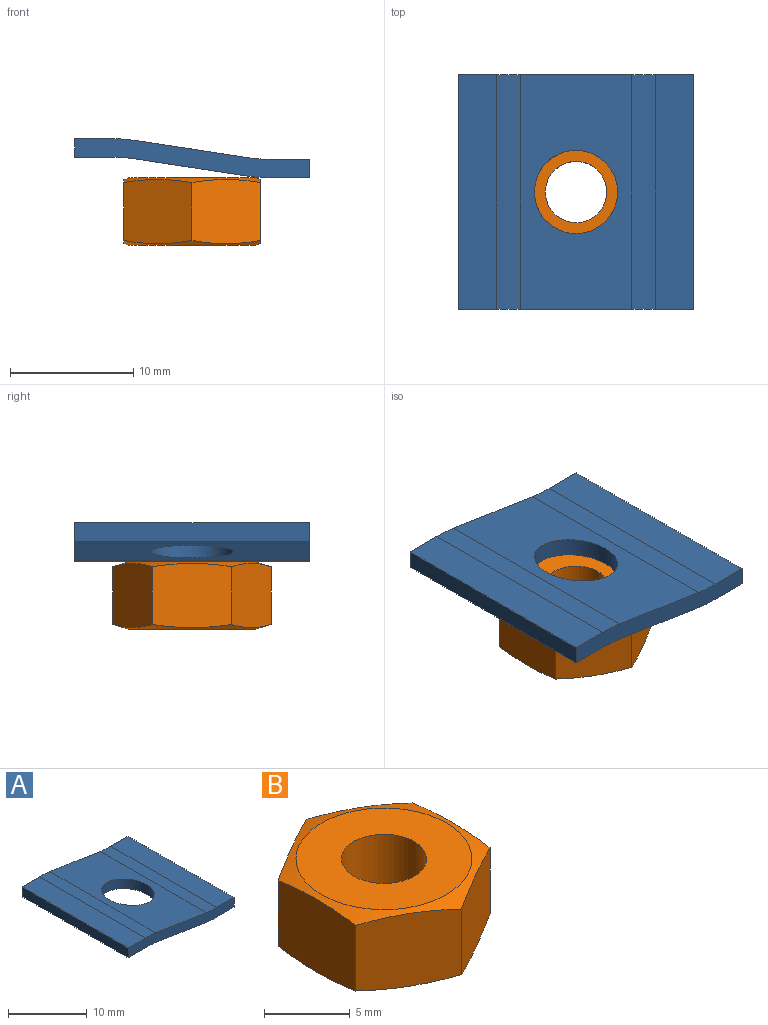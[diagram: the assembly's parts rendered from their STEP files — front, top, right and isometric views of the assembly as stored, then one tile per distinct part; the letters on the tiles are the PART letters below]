
ASSEMBLY  parts=2 mates=2
PART A: 15 faces, bbox 19.1x19.1x3.2 mm
  f0: plane 19.05x3.09mm, normal (0,0,1), area 58.8mm2, adj f1,f8,f9,f13
  f1: plane 19.05x1.5mm, normal (-1,0,0), area 28.5mm2, adj f0,f2,f8,f9
  f2: plane 19.05x3.09mm, normal (0,0,-1), area 58.8mm2, adj f1,f8,f9,f10
  f3: plane 19.05x9.03mm, normal (-0.15,0,-0.99), area 137.9mm2, adj f8,f9,f10,f11,f14
  f4: plane 19.05x3.09mm, normal (0,0,-1), area 58.8mm2, adj f5,f8,f9,f11
  f5: plane 19.05x1.5mm, normal (1,0,0), area 28.5mm2, adj f4,f6,f8,f9
  f6: plane 19.05x3.09mm, normal (0,0,1), area 58.8mm2, adj f5,f8,f9,f12
  f7: plane 19.05x9.03mm, normal (0.15,0,0.99), area 137.9mm2, adj f8,f9,f12,f13,f14
  f8: plane 19.05x3.18mm, normal (0,-1,0), area 28.5mm2, adj f0,f1,f2,f3,f4,f5,f6,f7
  f9: plane 19.05x3.18mm, normal (0,1,0), area 28.5mm2, adj f0,f1,f2,f3,f4,f5,f6,f7
  f10: cylinder r=12.7mm len=19.05mm, axis (0,-1,0), area 36.8mm2, adj f2,f3,f8,f9
  f11: cylinder r=12.7mm len=19.05mm, axis (0,1,0), area 36.8mm2, adj f3,f4,f8,f9
  f12: cylinder r=12.7mm len=19.05mm, axis (0,-1,0), area 36.8mm2, adj f6,f7,f8,f9
  f13: cylinder r=12.7mm len=19.05mm, axis (0,1,0), area 36.8mm2, adj f0,f7,f8,f9
  f14: cylinder r=3.37mm len=6.75mm, axis (0,0,-1), area 31.8mm2, adj f3,f7
PART B: 11 faces, bbox 12.8x12.8x5.5 mm
  f0: plane 6.42x5.22mm, normal (1,0,0), area 32.3mm2, adj f1,f5,f9,f10
  f1: plane 5.56x5.21mm, normal (0.5,-0.87,0), area 32.3mm2, adj f0,f2,f9,f10
  f2: plane 5.56x5.21mm, normal (-0.5,-0.87,0), area 32.3mm2, adj f1,f3,f9,f10
  f3: plane 6.42x5.22mm, normal (-1,0,0), area 32.3mm2, adj f2,f4,f9,f10
  f4: plane 5.56x5.21mm, normal (-0.5,0.87,0), area 32.3mm2, adj f3,f5,f9,f10
  f5: plane 5.56x5.21mm, normal (0.5,0.87,0), area 32.3mm2, adj f0,f4,f9,f10
  f6: cylinder r=2.49mm len=5.46mm, axis (0,0,-1), area 85.4mm2, adj f7,f8
  f7: plane 10.29x10.29mm, normal (0,0,1), area 63.7mm2, adj f6,f10
  f8: plane 10.29x10.29mm, normal (0,0,-1), area 63.7mm2, adj f6,f9
  f9: cone r=6.42mm half-angle=73.3deg, axis (0,0,1), area 24.8mm2, adj f0,f1,f2,f3,f4,f5,f8
  f10: cone r=6.42mm half-angle=73.3deg, axis (0,0,-1), area 24.8mm2, adj f0,f1,f2,f3,f4,f5,f7
PLACE A rot(axis=(0,0,-1),0deg) t=(18.71,2.11,42.59)mm
PLACE B rot(axis=(0,0,-1),0deg) t=(18.71,2.11,51.41)mm
MATE planar B.f9 <-> A.f4  axis (0,0,1) through (-67.01,2.11,37.92)mm
MATE cylindrical A.f14 <-> B.f6  axis (0,0,-1) through (-67.01,2.11,40.79)mm
